# Revit family: Drain_Floor_12_Inch_Square_Open_Top_Zurn-Z566
name_source: partatom
category: Plumbing Fixtures
units: mm (PartAtom-declared; Revit-internal decimal feet)

## family parameters
Always vertical = Yes
Cut with Voids When Loaded = No
Maintain Annotation Orientation = No
OmniClass Number = 23.70.50.21.24
OmniClass Title = Waste Water Drains
Part Type = Normal
Room Calculation Point = No
Round Connector Dimension = Use Radius
Shared = No
Work Plane-Based = No

## types (10) — shared parameters
Approx. Weight (Lbs) = 42
Assembly Code = D2030300
CW Connection = No
Default Elevation = 0' - 0"
Description = 12 Inch Square Open Top Drain
HW Connection = No
Main Material = Iron - Zurn - Cast - Painted - Blue
Manufacturer = Zurn Water, LLC
Manufacurer Brand = Zurn
Model = Z566
Product Documentation Link = https://files.zurn.com
Product Page URL = https://www.zurn.com
Product data url = https://bimobject.com
URL = www.zurn.com
Veneer Top = Bronze - Zurn-Polished Nickel
Vent Connection = No
Waste Connection = Yes

## per-type parameters (varying)
| type | Body Height | Flange | NB Top | Outlet Outer Radius | Outlet Radius | Top | Type Comments |
| Z566-3NL Outlet | 0' - 11 11/32" | 0' - 0 3/8" | No | 0' - 2 7/32" | 0' - 1 1/2" | Yes | Z566-3NL (Neo-Loc Outlet) |
| ZN566-3NL Outlet | 0' - 11 11/32" | 0' - 0 9/16" | Yes | 0' - 2 7/32" | 0' - 1 1/2" | No | ZN566-3NL (Neo_Loc Outlet) |
| Z566-2NL Outlet | 0' - 10 1/4" | 0' - 0 3/8" | No | 0' - 1 11/16" | 0' - 1" | Yes | Z566-3NL (Neo-Loc Outlet) |
| Z566-4NL Outlet | 1' - 0 11/32" | 0' - 0 3/8" | No | 0' - 2 27/32" | 0' - 2" | Yes | Z566-4NL (Neo-Loc Outlet) |
| Z566-3IP Outlet | 0' - 7 3/4" | 0' - 0 3/8" | No | 0' - 2 1/4" | 0' - 1 1/2" | Yes | Z566-3IP (Threaded Outlet) |
| Z566-4IP Outlet | 0' - 7 15/16" | 0' - 0 3/8" | No | 0' - 2 13/16" | 0' - 2" | Yes | Z566-4IP (Threaded Outlet) |
| ZN566-2NL Outlet | 0' - 10 1/4" | 0' - 0 9/16" | Yes | 0' - 1 11/16" | 0' - 1" | No | Z566-2NL (Neo-Loc Outlet) |
| ZN566-4NL Outlet | 1' - 0 7/32" | 0' - 0 11/16" | Yes | 0' - 2 27/32" | 0' - 2" | No | ZN566-4NL (Neo-Loc Outlet) |
| ZN566-3IP Outlet | 0' - 7 3/4" | 0' - 0 9/16" | Yes | 0' - 2 1/4" | 0' - 1 1/2" | No | ZN566-3IP (Threaded Outlet) |
| ZN566-4IP Outlet | 0' - 7 15/16" | 0' - 0 9/16" | Yes | 0' - 2 13/16" | 0' - 2" | No | ZN566-4IP (Threaded Outlet) |

## geometry (parser evidence)
native form markers: Sweep x2
no freeform markers — native parametric forms only
